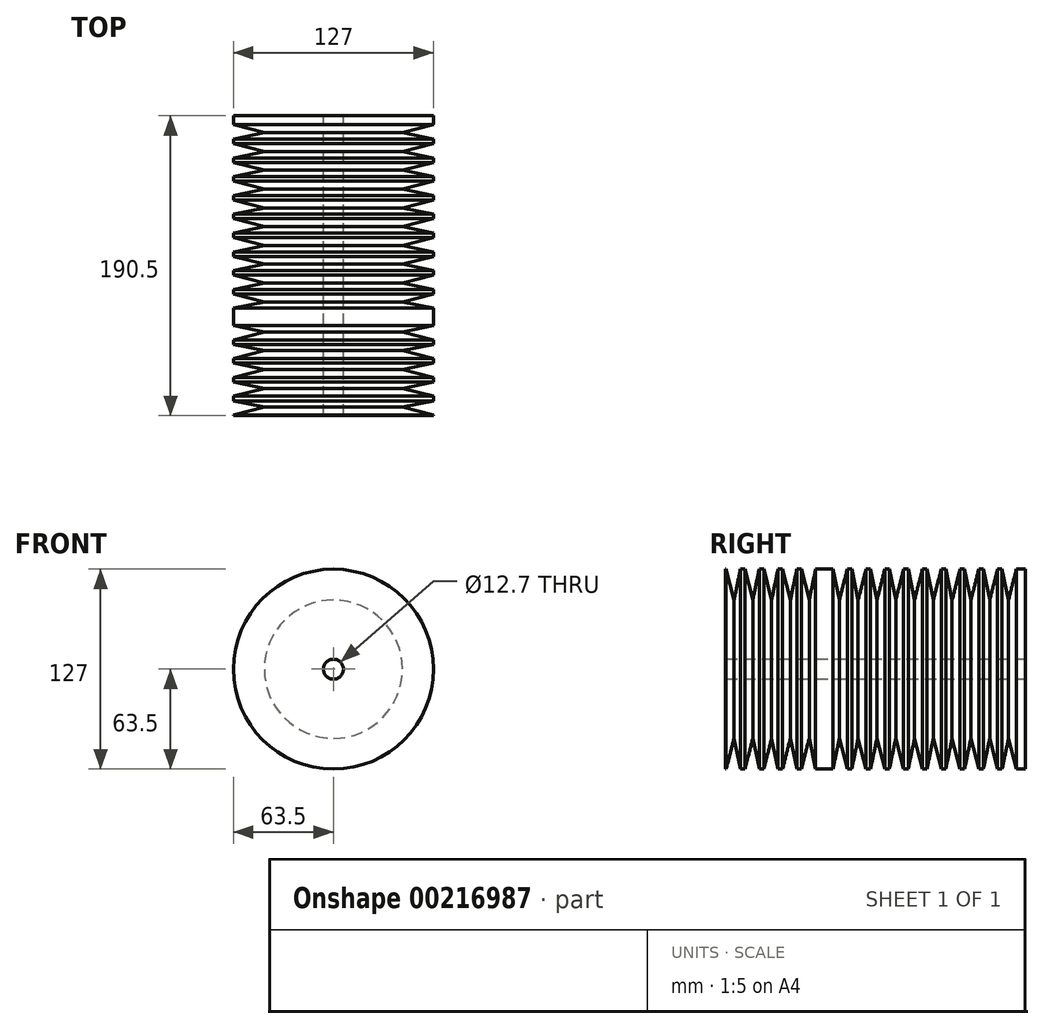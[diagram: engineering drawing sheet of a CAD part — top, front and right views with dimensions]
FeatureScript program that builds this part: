
annotation { "Feature Type Name" : "Feature", "Feature Type Description" : "" }
export const myFeature = defineFeature(function(context is Context, id is Id, definition is map)
    precondition{}
    {
        {
            var Q0;
            Q0=qCreatedBy(makeId("Front.planeOp"),FACE);
            var sketch = newSketch(context, id + "F0", { "sketchPlane" : qUnion([Q0])});
            skCircle(sketch, "E0", {"center": v(0, 0) * mm, "radius": 63.5 * mm});
            skCircle(sketch, "E1", {"center": v(0, 0) * mm, "radius": 6.35 * mm});
            skSolve(sketch);
        }
        {
            var Q0;
            Q0=makeQuery(id+"F0.imprint","IMPRINT",FACE,{"disambiguationData":[TD([[makeQuery(id+"F0.imprint","IMPRINT",EDGE,{"derivedFrom":sQuery(id+"F0.wireOp",EDGE,"E0")}),1.0]])]});
            extrude(context, id + "F1", {"entities" : qUnion([Q0]), "depth" : 127 * mm});
        }
        {
            var Q0;
            Q0=qCreatedBy(makeId("Right.planeOp"),FACE);
            var sketch = newSketch(context, id + "F2", { "sketchPlane" : qUnion([Q0])});
            skLineSegment(sketch, "E2", {"start": v(0, 64.94) * mm, "end": v(-127.74, 64.94) * mm});
            skLineSegment(sketch, "E3", {"start": v(-5.36, 64.94) * mm, "end": v(-10.73, 43.9) * mm});
            skLineSegment(sketch, "E4", {"start": v(-10.73, 43.9) * mm, "end": v(-15.08, 64.94) * mm});
            skLineSegment(sketch, "E5.1.0.0", {"start": v(-17.3, 64.94) * mm, "end": v(-22.67, 43.9) * mm});
            skLineSegment(sketch, "E5.1.0.1", {"start": v(-22.67, 43.9) * mm, "end": v(-27.02, 64.94) * mm});
            skLineSegment(sketch, "E5.1.0.2", {"start": v(-11.94, 64.94) * mm, "end": v(-139.68, 64.94) * mm});
            skLineSegment(sketch, "E5.2.0.0", {"start": v(-29.24, 64.94) * mm, "end": v(-34.6, 43.9) * mm});
            skLineSegment(sketch, "E5.2.0.1", {"start": v(-34.6, 43.9) * mm, "end": v(-38.95, 64.94) * mm});
            skLineSegment(sketch, "E5.2.0.2", {"start": v(-23.88, 64.94) * mm, "end": v(-151.62, 64.94) * mm});
            skLineSegment(sketch, "E5.3.0.0", {"start": v(-41.17, 64.94) * mm, "end": v(-46.54, 43.9) * mm});
            skLineSegment(sketch, "E5.3.0.1", {"start": v(-46.54, 43.9) * mm, "end": v(-50.9, 64.94) * mm});
            skLineSegment(sketch, "E5.3.0.2", {"start": v(-35.81, 64.94) * mm, "end": v(-163.56, 64.94) * mm});
            skLineSegment(sketch, "E5.4.0.0", {"start": v(-53.11, 64.94) * mm, "end": v(-58.48, 43.9) * mm});
            skLineSegment(sketch, "E5.4.0.1", {"start": v(-58.48, 43.9) * mm, "end": v(-62.83, 64.94) * mm});
            skLineSegment(sketch, "E5.4.0.2", {"start": v(-47.75, 64.94) * mm, "end": v(-175.5, 64.94) * mm});
            skLineSegment(sketch, "E5.5.0.0", {"start": v(-65.05, 64.94) * mm, "end": v(-70.42, 43.9) * mm});
            skLineSegment(sketch, "E5.5.0.1", {"start": v(-70.42, 43.9) * mm, "end": v(-74.77, 64.94) * mm});
            skLineSegment(sketch, "E5.5.0.2", {"start": v(-59.7, 64.94) * mm, "end": v(-187.43, 64.94) * mm});
            skLineSegment(sketch, "E5.6.0.0", {"start": v(-76.99, 64.94) * mm, "end": v(-82.36, 43.9) * mm});
            skLineSegment(sketch, "E5.6.0.1", {"start": v(-82.36, 43.9) * mm, "end": v(-86.7, 64.94) * mm});
            skLineSegment(sketch, "E5.6.0.2", {"start": v(-71.63, 64.94) * mm, "end": v(-199.37, 64.94) * mm});
            skLineSegment(sketch, "E5.7.0.0", {"start": v(-88.93, 64.94) * mm, "end": v(-94.3, 43.9) * mm});
            skLineSegment(sketch, "E5.7.0.1", {"start": v(-94.3, 43.9) * mm, "end": v(-98.64, 64.94) * mm});
            skLineSegment(sketch, "E5.7.0.2", {"start": v(-83.57, 64.94) * mm, "end": v(-211.31, 64.94) * mm});
            skLineSegment(sketch, "E5.8.0.0", {"start": v(-100.86, 64.94) * mm, "end": v(-106.23, 43.9) * mm});
            skLineSegment(sketch, "E5.8.0.1", {"start": v(-106.23, 43.9) * mm, "end": v(-110.58, 64.94) * mm});
            skLineSegment(sketch, "E5.8.0.2", {"start": v(-95.5, 64.94) * mm, "end": v(-223.25, 64.94) * mm});
            skLineSegment(sketch, "E5.9.0.0", {"start": v(-112.8, 64.94) * mm, "end": v(-118.17, 43.9) * mm});
            skLineSegment(sketch, "E5.9.0.1", {"start": v(-118.17, 43.9) * mm, "end": v(-122.52, 64.94) * mm});
            skLineSegment(sketch, "E5.9.0.2", {"start": v(-107.44, 64.94) * mm, "end": v(-235.19, 64.94) * mm});
            skLineSegment(sketch, "E5.direction1", {"start": v(-10.73, 43.9) * mm, "end": v(-22.67, 43.9) * mm, "construction": true});
            skLineSegment(sketch, "E6", {"start": v(-127.74, 64.94) * mm, "end": v(-127.74, -5.8) * mm, "construction": true});
            skLineSegment(sketch, "E7.MirrorCS", {"start": v(-137.32, 43.9) * mm, "end": v(-132.97, 64.94) * mm});
            skLineSegment(sketch, "E8.MirrorCS", {"start": v(-142.69, 64.94) * mm, "end": v(-137.32, 43.9) * mm});
            skLineSegment(sketch, "E9.MirrorCS", {"start": v(-149.26, 43.9) * mm, "end": v(-144.9, 64.94) * mm});
            skLineSegment(sketch, "E10.MirrorCS", {"start": v(-154.63, 64.94) * mm, "end": v(-149.26, 43.9) * mm});
            skLineSegment(sketch, "E11.MirrorCS", {"start": v(-161.2, 43.9) * mm, "end": v(-156.85, 64.94) * mm});
            skLineSegment(sketch, "E12.MirrorCS", {"start": v(-166.56, 64.94) * mm, "end": v(-161.2, 43.9) * mm});
            skLineSegment(sketch, "E13.MirrorCS", {"start": v(-173.13, 43.9) * mm, "end": v(-168.78, 64.94) * mm});
            skLineSegment(sketch, "E14.MirrorCS", {"start": v(-178.5, 64.94) * mm, "end": v(-173.13, 43.9) * mm});
            skLineSegment(sketch, "E15.MirrorCS", {"start": v(-185.07, 43.9) * mm, "end": v(-180.72, 64.94) * mm});
            skLineSegment(sketch, "E16.MirrorCS", {"start": v(-190.44, 64.94) * mm, "end": v(-185.07, 43.9) * mm});
            skLineSegment(sketch, "E17.MirrorCS", {"start": v(-197, 43.9) * mm, "end": v(-192.66, 64.94) * mm});
            skLineSegment(sketch, "E18.MirrorCS", {"start": v(-202.38, 64.94) * mm, "end": v(-197, 43.9) * mm});
            skLineSegment(sketch, "E19.MirrorCS", {"start": v(-208.95, 43.9) * mm, "end": v(-204.6, 64.94) * mm});
            skLineSegment(sketch, "E20.MirrorCS", {"start": v(-214.32, 64.94) * mm, "end": v(-208.95, 43.9) * mm});
            skLineSegment(sketch, "E21.MirrorCS", {"start": v(-220.88, 43.9) * mm, "end": v(-216.54, 64.94) * mm});
            skLineSegment(sketch, "E22.MirrorCS", {"start": v(-226.25, 64.94) * mm, "end": v(-220.88, 43.9) * mm});
            skLineSegment(sketch, "E23.MirrorCS", {"start": v(-232.82, 43.9) * mm, "end": v(-228.47, 64.94) * mm});
            skLineSegment(sketch, "E24.MirrorCS", {"start": v(-238.2, 64.94) * mm, "end": v(-232.82, 43.9) * mm});
            skLineSegment(sketch, "E25.MirrorCS", {"start": v(-244.76, 43.9) * mm, "end": v(-240.41, 64.94) * mm});
            skSolve(sketch);
        }
        {
            var Q0;
            {var subQ3=sQuery(id+"F2.wireOp",EDGE,"E3");Q0=makeQuery(id+"F2.imprint","IMPRINT",FACE,{"disambiguationData":[TD([[makeQuery(id+"F2.imprint","IMPRINT",EDGE,{"derivedFrom":subQ3}),-1.0]])]});}
            var Q1;
            {var subQ0=sQuery(id+"F2.wireOp",EDGE,"E5.1.0.0");Q1=makeQuery(id+"F2.imprint","IMPRINT",FACE,{"disambiguationData":[TD([[makeQuery(id+"F2.imprint","IMPRINT",EDGE,{"derivedFrom":subQ0}),-1.0]])]});}
            var Q2;
            {var subQ0=sQuery(id+"F2.wireOp",EDGE,"E5.2.0.0");Q2=makeQuery(id+"F2.imprint","IMPRINT",FACE,{"disambiguationData":[TD([[makeQuery(id+"F2.imprint","IMPRINT",EDGE,{"derivedFrom":subQ0}),-1.0]])]});}
            var Q3;
            {var subQ0=sQuery(id+"F2.wireOp",EDGE,"E5.3.0.0");Q3=makeQuery(id+"F2.imprint","IMPRINT",FACE,{"disambiguationData":[TD([[makeQuery(id+"F2.imprint","IMPRINT",EDGE,{"derivedFrom":subQ0}),-1.0]])]});}
            var Q4;
            {var subQ0=sQuery(id+"F2.wireOp",EDGE,"E5.4.0.0");Q4=makeQuery(id+"F2.imprint","IMPRINT",FACE,{"disambiguationData":[TD([[makeQuery(id+"F2.imprint","IMPRINT",EDGE,{"derivedFrom":subQ0}),-1.0]])]});}
            var Q5;
            {var subQ0=sQuery(id+"F2.wireOp",EDGE,"E5.5.0.0");Q5=makeQuery(id+"F2.imprint","IMPRINT",FACE,{"disambiguationData":[TD([[makeQuery(id+"F2.imprint","IMPRINT",EDGE,{"derivedFrom":subQ0}),-1.0]])]});}
            var Q6;
            {var subQ0=sQuery(id+"F2.wireOp",EDGE,"E5.6.0.0");Q6=makeQuery(id+"F2.imprint","IMPRINT",FACE,{"disambiguationData":[TD([[makeQuery(id+"F2.imprint","IMPRINT",EDGE,{"derivedFrom":subQ0}),-1.0]])]});}
            var Q7;
            {var subQ0=sQuery(id+"F2.wireOp",EDGE,"E5.7.0.0");Q7=makeQuery(id+"F2.imprint","IMPRINT",FACE,{"disambiguationData":[TD([[makeQuery(id+"F2.imprint","IMPRINT",EDGE,{"derivedFrom":subQ0}),-1.0]])]});}
            var Q8;
            {var subQ0=sQuery(id+"F2.wireOp",EDGE,"E5.8.0.0");Q8=makeQuery(id+"F2.imprint","IMPRINT",FACE,{"disambiguationData":[TD([[makeQuery(id+"F2.imprint","IMPRINT",EDGE,{"derivedFrom":subQ0}),-1.0]])]});}
            var Q9;
            {var subQ0=sQuery(id+"F2.wireOp",EDGE,"E5.9.0.0");Q9=makeQuery(id+"F2.imprint","IMPRINT",FACE,{"disambiguationData":[TD([[makeQuery(id+"F2.imprint","IMPRINT",EDGE,{"derivedFrom":subQ0}),-1.0]])]});}
            var Q10;
            {var subQ0=sQuery(id+"F2.wireOp",EDGE,"E7.MirrorCS");Q10=makeQuery(id+"F2.imprint","IMPRINT",FACE,{"disambiguationData":[TD([[makeQuery(id+"F2.imprint","IMPRINT",EDGE,{"derivedFrom":subQ0}),1.0]])]});}
            var Q11;
            {var subQ0=sQuery(id+"F2.wireOp",EDGE,"E9.MirrorCS");Q11=makeQuery(id+"F2.imprint","IMPRINT",FACE,{"disambiguationData":[TD([[makeQuery(id+"F2.imprint","IMPRINT",EDGE,{"derivedFrom":subQ0}),1.0]])]});}
            var Q12;
            {var subQ0=sQuery(id+"F2.wireOp",EDGE,"E11.MirrorCS");Q12=makeQuery(id+"F2.imprint","IMPRINT",FACE,{"disambiguationData":[TD([[makeQuery(id+"F2.imprint","IMPRINT",EDGE,{"derivedFrom":subQ0}),1.0]])]});}
            var Q13;
            {var subQ0=sQuery(id+"F2.wireOp",EDGE,"E13.MirrorCS");Q13=makeQuery(id+"F2.imprint","IMPRINT",FACE,{"disambiguationData":[TD([[makeQuery(id+"F2.imprint","IMPRINT",EDGE,{"derivedFrom":subQ0}),1.0]])]});}
            var Q14;
            {var subQ0=sQuery(id+"F2.wireOp",EDGE,"E15.MirrorCS");Q14=makeQuery(id+"F2.imprint","IMPRINT",FACE,{"disambiguationData":[TD([[makeQuery(id+"F2.imprint","IMPRINT",EDGE,{"derivedFrom":subQ0}),1.0]])]});}
            var Q15;
            {var subQ0=sQuery(id+"F2.wireOp",EDGE,"E17.MirrorCS");Q15=makeQuery(id+"F2.imprint","IMPRINT",FACE,{"disambiguationData":[TD([[makeQuery(id+"F2.imprint","IMPRINT",EDGE,{"derivedFrom":subQ0}),1.0]])]});}
            var Q16;
            Q16=makeQuery(id+"F1.opExtrude","CAP_EDGE",EDGE,{"disambiguationData":[OSD([sQuery(id+"F0.wireOp",EDGE,"E0")])],"isStart":false});
            revolve(context, id + "F3", {"operationType" : NewBodyOperationType.REMOVE, "entities" : qUnion([Q0, Q1, Q2, Q3, Q4, Q5, Q6, Q7, Q8, Q9, Q10, Q11, Q12, Q13, Q14, Q15]), "axis" : qUnion([Q16]), "revolveType" : RevolveType.FULL, "oppositeDirection" : true});
        }
        {
            var Q0;
            Q0=makeQuery(id+"F1.opExtrude","CAP_FACE",FACE,{"disambiguationData":[OSD([sQuery(id+"F0.wireOp",EDGE,"E0"),sQuery(id+"F0.wireOp",EDGE,"E1")])],"isStart":false});
            extrude(context, id + "F4", {"entities" : qUnion([Q0]), "operationType" : NewBodyOperationType.ADD, "depth" : 63.5 * mm});
        }
        {
            var Q0;
            {var subQ0=sQuery(id+"F2.wireOp",EDGE,"E7.MirrorCS");Q0=makeQuery(id+"F2.imprint","IMPRINT",FACE,{"disambiguationData":[TD([[makeQuery(id+"F2.imprint","IMPRINT",EDGE,{"derivedFrom":subQ0}),1.0]])]});}
            var Q1;
            Q1 = qSketchRegion(id + "F2", true);
            var Q2;
            Q2=makeQuery(id+"F4.opExtrude","CAP_EDGE",EDGE,{"disambiguationData":[OSD([sQuery(id+"F0.wireOp",EDGE,"E0")])],"isStart":false});
            revolve(context, id + "F5", {"operationType" : NewBodyOperationType.REMOVE, "entities" : qUnion([Q0, Q1]), "axis" : qUnion([Q2]), "revolveType" : RevolveType.FULL, "oppositeDirection" : true});
        }
    });
